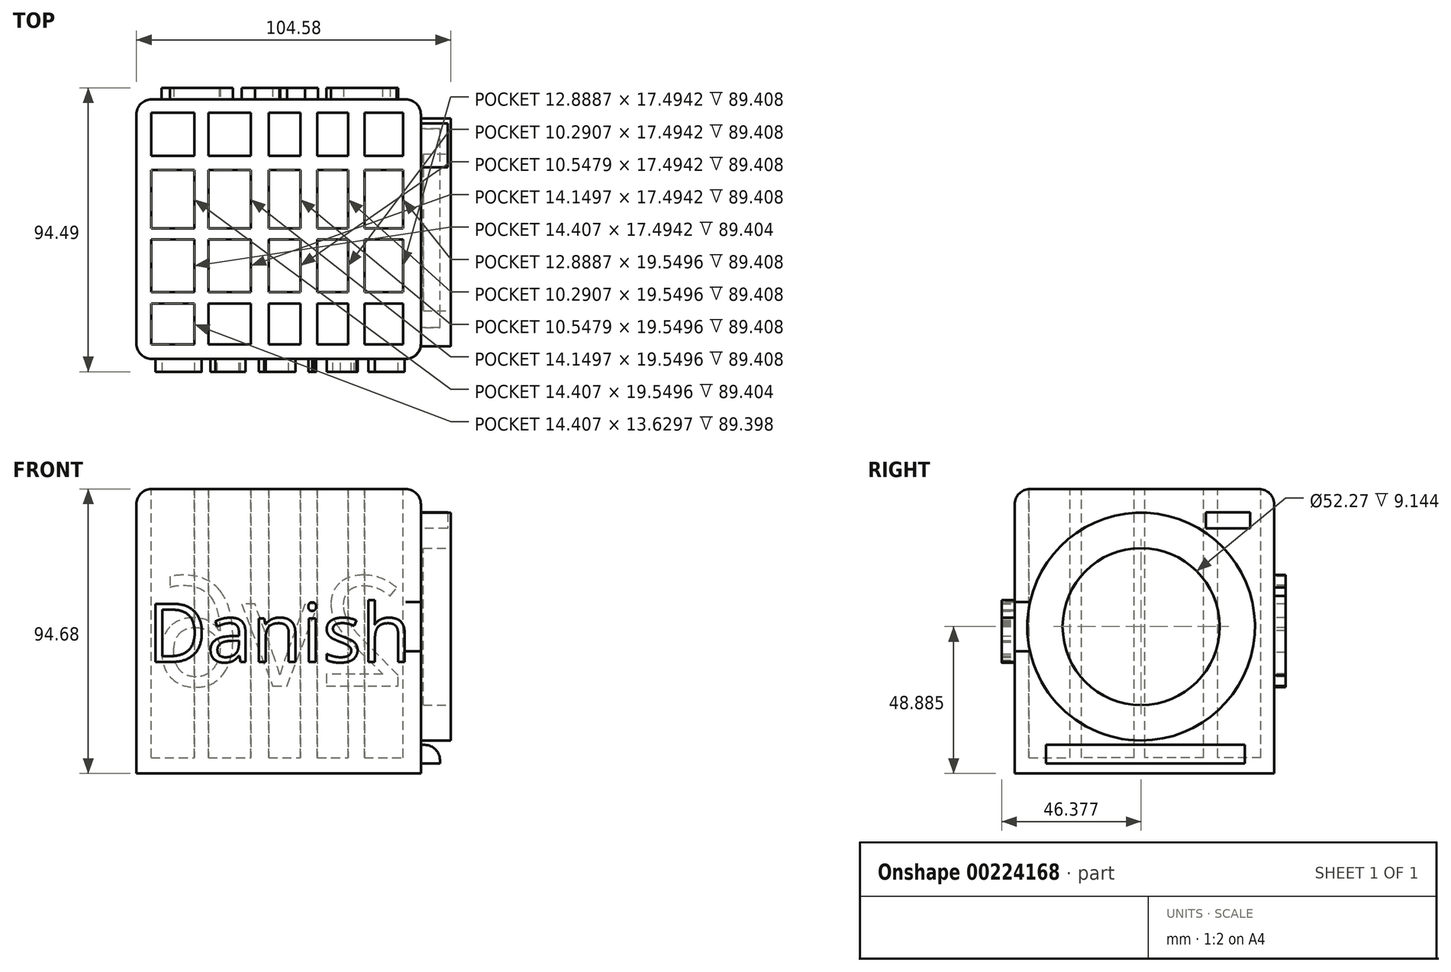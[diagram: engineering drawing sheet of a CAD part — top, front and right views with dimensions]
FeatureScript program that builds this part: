
annotation { "Feature Type Name" : "Feature", "Feature Type Description" : "" }
export const myFeature = defineFeature(function(context is Context, id is Id, definition is map)
    precondition{}
    {
        {
            var Q0;
            Q0=qCreatedBy(makeId("Front.planeOp"),FACE);
            var sketch = newSketch(context, id + "F0", { "sketchPlane" : qUnion([Q0])});
            skLineSegment(sketch, "E0.bottom", {"start": v(-44, 40.39) * mm, "end": v(50.68, 40.39) * mm});
            skLineSegment(sketch, "E0.top", {"start": v(-44, -54.29) * mm, "end": v(50.68, -54.29) * mm});
            skLineSegment(sketch, "E0.left", {"start": v(-44, 40.39) * mm, "end": v(-44, -54.29) * mm});
            skLineSegment(sketch, "E0.right", {"start": v(50.68, 40.39) * mm, "end": v(50.68, -54.29) * mm});
            skSolve(sketch);
        }
        {
            var Q0;
            Q0=makeQuery(id+"F0.imprint","IMPRINT",FACE,{"disambiguationData":[TD([[makeQuery(id+"F0.imprint","IMPRINT",EDGE,{"derivedFrom":sQuery(id+"F0.wireOp",EDGE,"E0.bottom")}),-1.0]])]});
            extrude(context, id + "F1", {"entities" : qUnion([Q0]), "depth" : 50.3 * mm});
        }
        {
            var Q0;
            Q0=makeQuery(id+"F1.opExtrude","CAP_FACE",FACE,{"disambiguationData":[OSD([sQuery(id+"F0.wireOp",EDGE,"E0.bottom"),sQuery(id+"F0.wireOp",EDGE,"E0.top"),sQuery(id+"F0.wireOp",EDGE,"E0.left"),sQuery(id+"F0.wireOp",EDGE,"E0.right")])],"isStart":true});
            extrude(context, id + "F2", {"entities" : qUnion([Q0]), "operationType" : NewBodyOperationType.ADD, "depth" : 36.07 * mm});
        }
        {
            var Q0;
            {var subQ0=sQuery(id+"F0.wireOp",EDGE,"E0.bottom");Q0=makeQuery(id+"F2.boolean.opBoolean","MERGE",FACE,{"derivedFrom":[makeQuery(id+"F1.opExtrude","SWEPT_FACE",FACE,{"disambiguationData":[OSD([subQ0])]}),makeQuery(id+"F2.opExtrude","SWEPT_FACE",FACE,{"disambiguationData":[OSD([subQ0])]})]});}
            var sketch = newSketch(context, id + "F3", { "sketchPlane" : qUnion([Q0])});
            skLineSegment(sketch, "E1.bottom", {"start": v(-39.1, 31.64) * mm, "end": v(44.79, 31.64) * mm});
            skLineSegment(sketch, "E1.top", {"start": v(-39.1, -45.53) * mm, "end": v(44.79, -45.53) * mm});
            skLineSegment(sketch, "E1.left", {"start": v(-39.1, 31.64) * mm, "end": v(-39.1, -45.53) * mm});
            skLineSegment(sketch, "E1.right", {"start": v(44.79, 31.64) * mm, "end": v(44.79, -45.53) * mm});
            skSolve(sketch);
        }
        {
            var Q0;
            Q0=makeQuery(id+"F3.imprint","IMPRINT",FACE,{"disambiguationData":[TD([[makeQuery(id+"F3.imprint","IMPRINT",EDGE,{"derivedFrom":sQuery(id+"F3.wireOp",EDGE,"E1.bottom")}),-1.0]])]});
            extrude(context, id + "F4", {"entities" : qUnion([Q0]), "operationType" : NewBodyOperationType.REMOVE, "oppositeDirection" : true, "depth" : 89.4 * mm});
        }
        {
            var Q0;
            Q0=makeQuery(id+"F4.boolean.opBoolean","COPY",FACE,{"derivedFrom":makeQuery(id+"F4.opExtrude","CAP_FACE",FACE,{"disambiguationData":[OSD([sQuery(id+"F3.wireOp",EDGE,"E1.bottom"),sQuery(id+"F3.wireOp",EDGE,"E1.top"),sQuery(id+"F3.wireOp",EDGE,"E1.left"),sQuery(id+"F3.wireOp",EDGE,"E1.right")])],"isStart":false})});
            var sketch = newSketch(context, id + "F5", { "sketchPlane" : qUnion([Q0])});
            skLineSegment(sketch, "E2.bottom", {"start": v(-24.7, -45.53) * mm, "end": v(-20.07, -45.53) * mm});
            skLineSegment(sketch, "E2.top", {"start": v(-24.7, 31.64) * mm, "end": v(-20.07, 31.64) * mm});
            skLineSegment(sketch, "E2.left", {"start": v(-24.7, -45.53) * mm, "end": v(-24.7, 31.64) * mm});
            skLineSegment(sketch, "E2.right", {"start": v(-20.07, -45.53) * mm, "end": v(-20.07, 31.64) * mm});
            skLineSegment(sketch, "E3.bottom", {"start": v(0, -45.53) * mm, "end": v(-5.92, -45.53) * mm});
            skLineSegment(sketch, "E3.top", {"start": v(0, 31.64) * mm, "end": v(-5.92, 31.64) * mm});
            skLineSegment(sketch, "E3.left", {"start": v(0, -45.53) * mm, "end": v(0, 31.64) * mm});
            skLineSegment(sketch, "E3.right", {"start": v(-5.92, -45.53) * mm, "end": v(-5.92, 31.64) * mm});
            skLineSegment(sketch, "E4.bottom", {"start": v(16.2, -45.53) * mm, "end": v(10.55, -45.53) * mm});
            skLineSegment(sketch, "E4.top", {"start": v(16.2, 31.64) * mm, "end": v(10.55, 31.64) * mm});
            skLineSegment(sketch, "E4.left", {"start": v(16.2, -45.53) * mm, "end": v(16.2, 31.64) * mm});
            skLineSegment(sketch, "E4.right", {"start": v(10.55, -45.53) * mm, "end": v(10.55, 31.64) * mm});
            skLineSegment(sketch, "E5.bottom", {"start": v(31.9, -45.53) * mm, "end": v(26.5, -45.53) * mm});
            skLineSegment(sketch, "E5.top", {"start": v(31.9, 31.64) * mm, "end": v(26.5, 31.64) * mm});
            skLineSegment(sketch, "E5.left", {"start": v(31.9, -45.53) * mm, "end": v(31.9, 31.64) * mm});
            skLineSegment(sketch, "E5.right", {"start": v(26.5, -45.53) * mm, "end": v(26.5, 31.64) * mm});
            skSolve(sketch);
        }
        {
            var Q0;
            Q0=makeQuery(id+"F5.imprint","IMPRINT",FACE,{"disambiguationData":[TD([[makeQuery(id+"F5.imprint","IMPRINT",EDGE,{"derivedFrom":sQuery(id+"F5.wireOp",EDGE,"E2.bottom")}),1.0]])]});
            var Q1;
            Q1=makeQuery(id+"F5.imprint","IMPRINT",FACE,{"disambiguationData":[TD([[makeQuery(id+"F5.imprint","IMPRINT",EDGE,{"derivedFrom":sQuery(id+"F5.wireOp",EDGE,"E3.bottom")}),1.0]])]});
            var Q2;
            Q2=makeQuery(id+"F5.imprint","IMPRINT",FACE,{"disambiguationData":[TD([[makeQuery(id+"F5.imprint","IMPRINT",EDGE,{"derivedFrom":sQuery(id+"F5.wireOp",EDGE,"E4.bottom")}),1.0]])]});
            var Q3;
            Q3=makeQuery(id+"F5.imprint","IMPRINT",FACE,{"disambiguationData":[TD([[makeQuery(id+"F5.imprint","IMPRINT",EDGE,{"derivedFrom":sQuery(id+"F5.wireOp",EDGE,"E5.bottom")}),1.0]])]});
            extrude(context, id + "F6", {"entities" : qUnion([Q0, Q1, Q2, Q3]), "operationType" : NewBodyOperationType.ADD, "depth" : 89.4 * mm});
        }
        {
            var Q0;
            {var subQ0=sQuery(id+"F0.wireOp",EDGE,"E0.bottom");Q0=makeQuery(id+"F6.boolean.opBoolean","MERGE",FACE,{"derivedFrom":[makeQuery(id+"F2.boolean.opBoolean","MERGE",FACE,{"derivedFrom":[makeQuery(id+"F1.opExtrude","SWEPT_FACE",FACE,{"disambiguationData":[OSD([subQ0])]}),makeQuery(id+"F2.opExtrude","SWEPT_FACE",FACE,{"disambiguationData":[OSD([subQ0])]})]}),makeQuery(id+"F6.opExtrude","CAP_FACE",FACE,{"disambiguationData":[OSD([sQuery(id+"F5.wireOp",EDGE,"E2.bottom"),sQuery(id+"F5.wireOp",EDGE,"E2.top"),sQuery(id+"F5.wireOp",EDGE,"E2.left"),sQuery(id+"F5.wireOp",EDGE,"E2.right")])],"isStart":false}),makeQuery(id+"F6.opExtrude","CAP_FACE",FACE,{"disambiguationData":[OSD([sQuery(id+"F5.wireOp",EDGE,"E3.bottom"),sQuery(id+"F5.wireOp",EDGE,"E3.top"),sQuery(id+"F5.wireOp",EDGE,"E3.left"),sQuery(id+"F5.wireOp",EDGE,"E3.right")])],"isStart":false}),makeQuery(id+"F6.opExtrude","CAP_FACE",FACE,{"disambiguationData":[OSD([sQuery(id+"F5.wireOp",EDGE,"E4.bottom"),sQuery(id+"F5.wireOp",EDGE,"E4.top"),sQuery(id+"F5.wireOp",EDGE,"E4.left"),sQuery(id+"F5.wireOp",EDGE,"E4.right")])],"isStart":false}),makeQuery(id+"F6.opExtrude","CAP_FACE",FACE,{"disambiguationData":[OSD([sQuery(id+"F5.wireOp",EDGE,"E5.bottom"),sQuery(id+"F5.wireOp",EDGE,"E5.top"),sQuery(id+"F5.wireOp",EDGE,"E5.left"),sQuery(id+"F5.wireOp",EDGE,"E5.right")])],"isStart":false})]});}
            var sketch = newSketch(context, id + "F7", { "sketchPlane" : qUnion([Q0])});
            skLineSegment(sketch, "E6.bottom", {"start": v(-39.1, 17.23) * mm, "end": v(44.79, 17.23) * mm});
            skLineSegment(sketch, "E6.top", {"start": v(-39.1, 12.6) * mm, "end": v(44.79, 12.6) * mm});
            skLineSegment(sketch, "E6.left", {"start": v(-39.1, 17.23) * mm, "end": v(-39.1, 12.6) * mm});
            skLineSegment(sketch, "E6.right", {"start": v(44.79, 17.23) * mm, "end": v(44.79, 12.6) * mm});
            skLineSegment(sketch, "E7.bottom", {"start": v(-39.1, -6.95) * mm, "end": v(47.08, -6.95) * mm});
            skLineSegment(sketch, "E7.top", {"start": v(-39.1, -10.55) * mm, "end": v(47.08, -10.55) * mm});
            skLineSegment(sketch, "E7.left", {"start": v(-39.1, -6.95) * mm, "end": v(-39.1, -10.55) * mm});
            skLineSegment(sketch, "E7.right", {"start": v(47.08, -6.95) * mm, "end": v(47.08, -10.55) * mm});
            skLineSegment(sketch, "E8.bottom", {"start": v(-39.1, -28.04) * mm, "end": v(44.79, -28.04) * mm});
            skLineSegment(sketch, "E8.top", {"start": v(-39.1, -31.9) * mm, "end": v(44.79, -31.9) * mm});
            skLineSegment(sketch, "E8.left", {"start": v(-39.1, -28.04) * mm, "end": v(-39.1, -31.9) * mm});
            skLineSegment(sketch, "E8.right", {"start": v(44.79, -28.04) * mm, "end": v(44.79, -31.9) * mm});
            skSolve(sketch);
        }
        {
            var Q0;
            {var subQ0=sQuery(id+"F7.wireOp",EDGE,"E6.left");Q0=makeQuery(id+"F7.imprint","IMPRINT",FACE,{"disambiguationData":[TD([[makeQuery(id+"F7.imprint","IMPRINT",EDGE,{"derivedFrom":subQ0}),1.0]])]});}
            var Q1;
            {var subQ0=sQuery(id+"F7.wireOp",EDGE,"E6.bottom");var subQ1=makeQuery(id+"F6.opExtrude","CAP_EDGE",EDGE,{"disambiguationData":[OSD([sQuery(id+"F5.wireOp",EDGE,"E2.right")])],"isStart":false});var subQ2=makeQuery(id+"F7.imprint","INTERSECT",VERTEX,{"derivedFrom":[subQ1,subQ0]});Q1=makeQuery(id+"F7.imprint","IMPRINT",FACE,{"disambiguationData":[TD([[makeQuery(id+"F7.imprint","IMPRINT",EDGE,{"disambiguationData":[TD([[subQ2,-1.0]])],"derivedFrom":subQ0}),-1.0]])]});}
            var Q2;
            {var subQ0=sQuery(id+"F7.wireOp",EDGE,"E6.bottom");var subQ1=makeQuery(id+"F6.opExtrude","CAP_EDGE",EDGE,{"disambiguationData":[OSD([sQuery(id+"F5.wireOp",EDGE,"E3.left")])],"isStart":false});var subQ2=makeQuery(id+"F7.imprint","INTERSECT",VERTEX,{"derivedFrom":[subQ1,subQ0]});Q2=makeQuery(id+"F7.imprint","IMPRINT",FACE,{"disambiguationData":[TD([[makeQuery(id+"F7.imprint","IMPRINT",EDGE,{"disambiguationData":[TD([[subQ2,-1.0]])],"derivedFrom":subQ0}),-1.0]])]});}
            var Q3;
            {var subQ0=sQuery(id+"F7.wireOp",EDGE,"E6.bottom");var subQ1=makeQuery(id+"F6.opExtrude","CAP_EDGE",EDGE,{"disambiguationData":[OSD([sQuery(id+"F5.wireOp",EDGE,"E4.left")])],"isStart":false});var subQ2=makeQuery(id+"F7.imprint","INTERSECT",VERTEX,{"derivedFrom":[subQ1,subQ0]});Q3=makeQuery(id+"F7.imprint","IMPRINT",FACE,{"disambiguationData":[TD([[makeQuery(id+"F7.imprint","IMPRINT",EDGE,{"disambiguationData":[TD([[subQ2,-1.0]])],"derivedFrom":subQ0}),-1.0]])]});}
            var Q4;
            {var subQ0=sQuery(id+"F7.wireOp",EDGE,"E6.right");Q4=makeQuery(id+"F7.imprint","IMPRINT",FACE,{"disambiguationData":[TD([[makeQuery(id+"F7.imprint","IMPRINT",EDGE,{"derivedFrom":subQ0}),-1.0]])]});}
            var Q5;
            {var subQ0=sQuery(id+"F7.wireOp",EDGE,"E7.bottom");var subQ1=makeQuery(id+"F6.opExtrude","CAP_EDGE",EDGE,{"disambiguationData":[OSD([sQuery(id+"F5.wireOp",EDGE,"E5.left")])],"isStart":false});var subQ2=makeQuery(id+"F7.imprint","INTERSECT",VERTEX,{"derivedFrom":[subQ1,subQ0]});Q5=makeQuery(id+"F7.imprint","IMPRINT",FACE,{"disambiguationData":[TD([[makeQuery(id+"F7.imprint","IMPRINT",EDGE,{"disambiguationData":[TD([[subQ2,-1.0]])],"derivedFrom":subQ0}),-1.0]])]});}
            var Q6;
            {var subQ0=sQuery(id+"F7.wireOp",EDGE,"E7.bottom");var subQ1=makeQuery(id+"F6.opExtrude","CAP_EDGE",EDGE,{"disambiguationData":[OSD([sQuery(id+"F5.wireOp",EDGE,"E4.left")])],"isStart":false});var subQ2=makeQuery(id+"F7.imprint","INTERSECT",VERTEX,{"derivedFrom":[subQ1,subQ0]});Q6=makeQuery(id+"F7.imprint","IMPRINT",FACE,{"disambiguationData":[TD([[makeQuery(id+"F7.imprint","IMPRINT",EDGE,{"disambiguationData":[TD([[subQ2,-1.0]])],"derivedFrom":subQ0}),-1.0]])]});}
            var Q7;
            {var subQ0=sQuery(id+"F7.wireOp",EDGE,"E7.bottom");var subQ1=makeQuery(id+"F6.opExtrude","CAP_EDGE",EDGE,{"disambiguationData":[OSD([sQuery(id+"F5.wireOp",EDGE,"E3.left")])],"isStart":false});var subQ2=makeQuery(id+"F7.imprint","INTERSECT",VERTEX,{"derivedFrom":[subQ1,subQ0]});Q7=makeQuery(id+"F7.imprint","IMPRINT",FACE,{"disambiguationData":[TD([[makeQuery(id+"F7.imprint","IMPRINT",EDGE,{"disambiguationData":[TD([[subQ2,-1.0]])],"derivedFrom":subQ0}),-1.0]])]});}
            var Q8;
            {var subQ0=sQuery(id+"F7.wireOp",EDGE,"E7.bottom");var subQ1=makeQuery(id+"F6.opExtrude","CAP_EDGE",EDGE,{"disambiguationData":[OSD([sQuery(id+"F5.wireOp",EDGE,"E2.right")])],"isStart":false});var subQ2=makeQuery(id+"F7.imprint","INTERSECT",VERTEX,{"derivedFrom":[subQ1,subQ0]});Q8=makeQuery(id+"F7.imprint","IMPRINT",FACE,{"disambiguationData":[TD([[makeQuery(id+"F7.imprint","IMPRINT",EDGE,{"disambiguationData":[TD([[subQ2,-1.0]])],"derivedFrom":subQ0}),-1.0]])]});}
            var Q9;
            {var subQ0=sQuery(id+"F7.wireOp",EDGE,"E7.left");Q9=makeQuery(id+"F7.imprint","IMPRINT",FACE,{"disambiguationData":[TD([[makeQuery(id+"F7.imprint","IMPRINT",EDGE,{"derivedFrom":subQ0}),1.0]])]});}
            var Q10;
            {var subQ0=sQuery(id+"F7.wireOp",EDGE,"E8.left");Q10=makeQuery(id+"F7.imprint","IMPRINT",FACE,{"disambiguationData":[TD([[makeQuery(id+"F7.imprint","IMPRINT",EDGE,{"derivedFrom":subQ0}),1.0]])]});}
            var Q11;
            {var subQ0=sQuery(id+"F7.wireOp",EDGE,"E8.bottom");var subQ1=makeQuery(id+"F6.opExtrude","CAP_EDGE",EDGE,{"disambiguationData":[OSD([sQuery(id+"F5.wireOp",EDGE,"E2.right")])],"isStart":false});var subQ2=makeQuery(id+"F7.imprint","INTERSECT",VERTEX,{"derivedFrom":[subQ1,subQ0]});Q11=makeQuery(id+"F7.imprint","IMPRINT",FACE,{"disambiguationData":[TD([[makeQuery(id+"F7.imprint","IMPRINT",EDGE,{"disambiguationData":[TD([[subQ2,-1.0]])],"derivedFrom":subQ0}),-1.0]])]});}
            var Q12;
            {var subQ0=sQuery(id+"F7.wireOp",EDGE,"E8.bottom");var subQ1=makeQuery(id+"F6.opExtrude","CAP_EDGE",EDGE,{"disambiguationData":[OSD([sQuery(id+"F5.wireOp",EDGE,"E3.left")])],"isStart":false});var subQ2=makeQuery(id+"F7.imprint","INTERSECT",VERTEX,{"derivedFrom":[subQ1,subQ0]});Q12=makeQuery(id+"F7.imprint","IMPRINT",FACE,{"disambiguationData":[TD([[makeQuery(id+"F7.imprint","IMPRINT",EDGE,{"disambiguationData":[TD([[subQ2,-1.0]])],"derivedFrom":subQ0}),-1.0]])]});}
            var Q13;
            {var subQ0=sQuery(id+"F7.wireOp",EDGE,"E8.bottom");var subQ1=makeQuery(id+"F6.opExtrude","CAP_EDGE",EDGE,{"disambiguationData":[OSD([sQuery(id+"F5.wireOp",EDGE,"E4.left")])],"isStart":false});var subQ2=makeQuery(id+"F7.imprint","INTERSECT",VERTEX,{"derivedFrom":[subQ1,subQ0]});Q13=makeQuery(id+"F7.imprint","IMPRINT",FACE,{"disambiguationData":[TD([[makeQuery(id+"F7.imprint","IMPRINT",EDGE,{"disambiguationData":[TD([[subQ2,-1.0]])],"derivedFrom":subQ0}),-1.0]])]});}
            var Q14;
            {var subQ0=sQuery(id+"F7.wireOp",EDGE,"E8.right");Q14=makeQuery(id+"F7.imprint","IMPRINT",FACE,{"disambiguationData":[TD([[makeQuery(id+"F7.imprint","IMPRINT",EDGE,{"derivedFrom":subQ0}),-1.0]])]});}
            extrude(context, id + "F8", {"entities" : qUnion([Q0, Q1, Q2, Q3, Q4, Q5, Q6, Q7, Q8, Q9, Q10, Q11, Q12, Q13, Q14]), "operationType" : NewBodyOperationType.ADD, "oppositeDirection" : true, "depth" : 91.44 * mm});
        }
        {
            var Q0;
            {var subQ0=sQuery(id+"F0.wireOp",EDGE,"E0.right");Q0=makeQuery(id+"F2.boolean.opBoolean","MERGE",FACE,{"derivedFrom":[makeQuery(id+"F1.opExtrude","SWEPT_FACE",FACE,{"disambiguationData":[OSD([subQ0])]}),makeQuery(id+"F2.opExtrude","SWEPT_FACE",FACE,{"disambiguationData":[OSD([subQ0])]})]});}
            var sketch = newSketch(context, id + "F9", { "sketchPlane" : qUnion([Q0])});
            skCircle(sketch, "E9", {"center": v(-8.23, -5.4) * mm, "radius": 37.89 * mm});
            skSolve(sketch);
        }
        {
            var Q0;
            Q0=makeQuery(id+"F9.imprint","IMPRINT",FACE,{"disambiguationData":[TD([[makeQuery(id+"F9.imprint","IMPRINT",EDGE,{"derivedFrom":sQuery(id+"F9.wireOp",EDGE,"E9")}),1.0]])]});
            extrude(context, id + "F10", {"entities" : qUnion([Q0]), "operationType" : NewBodyOperationType.ADD, "depth" : 9.9 * mm});
        }
        {
            var Q0;
            Q0=makeQuery(id+"F2.opExtrude","CAP_EDGE",EDGE,{"disambiguationData":[OSD([sQuery(id+"F0.wireOp",EDGE,"E0.bottom")])],"isStart":false});
            fillet(context, id + "F11", {"entities" : qUnion([Q0]), "radius" : 5.08 * mm, "tangentPropagation" : true, "allowEdgeOverflow" : false});
        }
        {
            var Q0;
            {var subQ0=sQuery(id+"F0.wireOp",EDGE,"E0.right");var subQ1=sQuery(id+"F0.wireOp",EDGE,"E0.bottom");Q0=makeQuery(id+"F2.boolean.opBoolean","MERGE",EDGE,{"derivedFrom":[makeQuery(id+"F1.opExtrude","SWEPT_EDGE",EDGE,{"disambiguationData":[OSD([subQ1,subQ0])]}),makeQuery(id+"F2.opExtrude","SWEPT_EDGE",EDGE,{"disambiguationData":[OSD([subQ1,subQ0])]})]});}
            fillet(context, id + "F12", {"entities" : qUnion([Q0]), "radius" : 5.08 * mm, "tangentPropagation" : true, "allowEdgeOverflow" : false});
        }
        {
            var Q0;
            Q0=makeQuery(id+"F1.opExtrude","CAP_EDGE",EDGE,{"disambiguationData":[OSD([sQuery(id+"F0.wireOp",EDGE,"E0.bottom")])],"isStart":false});
            fillet(context, id + "F13", {"entities" : qUnion([Q0]), "radius" : 5.08 * mm, "tangentPropagation" : true, "allowEdgeOverflow" : false});
        }
        {
            var Q0;
            {var subQ0=sQuery(id+"F0.wireOp",EDGE,"E0.left");var subQ1=sQuery(id+"F0.wireOp",EDGE,"E0.bottom");Q0=makeQuery(id+"F2.boolean.opBoolean","MERGE",EDGE,{"derivedFrom":[makeQuery(id+"F1.opExtrude","SWEPT_EDGE",EDGE,{"disambiguationData":[OSD([subQ1,subQ0])]}),makeQuery(id+"F2.opExtrude","SWEPT_EDGE",EDGE,{"disambiguationData":[OSD([subQ1,subQ0])]})]});}
            fillet(context, id + "F14", {"entities" : qUnion([Q0]), "radius" : 5.08 * mm, "tangentPropagation" : true, "allowEdgeOverflow" : false});
        }
        {
            var Q0;
            Q0=makeQuery(id+"F10.opExtrude","CAP_FACE",FACE,{"disambiguationData":[OSD([sQuery(id+"F9.wireOp",EDGE,"E9")])],"isStart":false});
            var sketch = newSketch(context, id + "F15", { "sketchPlane" : qUnion([Q0])});
            skCircle(sketch, "E10", {"center": v(-8.23, -5.4) * mm, "radius": 26.14 * mm});
            skSolve(sketch);
        }
        {
            var Q0;
            Q0=makeQuery(id+"F15.imprint","IMPRINT",FACE,{"disambiguationData":[TD([[makeQuery(id+"F15.imprint","IMPRINT",EDGE,{"derivedFrom":sQuery(id+"F15.wireOp",EDGE,"E10")}),1.0]])]});
            extrude(context, id + "F16", {"entities" : qUnion([Q0]), "operationType" : NewBodyOperationType.REMOVE, "oppositeDirection" : true, "depth" : 9.14 * mm});
        }
        {
            var Q0;
            {var subQ0=sQuery(id+"F0.wireOp",EDGE,"E0.right");Q0=makeQuery(id+"F2.boolean.opBoolean","MERGE",FACE,{"derivedFrom":[makeQuery(id+"F1.opExtrude","SWEPT_FACE",FACE,{"disambiguationData":[OSD([subQ0])]}),makeQuery(id+"F2.opExtrude","SWEPT_FACE",FACE,{"disambiguationData":[OSD([subQ0])]})]});}
            var sketch = newSketch(context, id + "F17", { "sketchPlane" : qUnion([Q0])});
            skLineSegment(sketch, "E11.bottom", {"start": v(13.38, 32.67) * mm, "end": v(28.04, 32.67) * mm});
            skLineSegment(sketch, "E11.top", {"start": v(13.38, 27.27) * mm, "end": v(28.04, 27.27) * mm});
            skLineSegment(sketch, "E11.left", {"start": v(13.38, 32.67) * mm, "end": v(13.38, 27.27) * mm});
            skLineSegment(sketch, "E11.right", {"start": v(28.04, 32.67) * mm, "end": v(28.04, 27.27) * mm});
            skSolve(sketch);
        }
        {
            var Q0;
            Q0=makeQuery(id+"F17.imprint","IMPRINT",FACE,{"disambiguationData":[TD([[makeQuery(id+"F17.imprint","IMPRINT",EDGE,{"derivedFrom":sQuery(id+"F17.wireOp",EDGE,"E11.bottom")}),-1.0]])]});
            extrude(context, id + "F18", {"entities" : qUnion([Q0]), "operationType" : NewBodyOperationType.ADD, "depth" : 8.9 * mm});
        }
        {
            var Q0;
            Q0=makeQuery(id+"F1.opExtrude","CAP_FACE",FACE,{"disambiguationData":[OSD([sQuery(id+"F0.wireOp",EDGE,"E0.bottom"),sQuery(id+"F0.wireOp",EDGE,"E0.top"),sQuery(id+"F0.wireOp",EDGE,"E0.left"),sQuery(id+"F0.wireOp",EDGE,"E0.right")])],"isStart":false});
            var sketch = newSketch(context, id + "F19", { "sketchPlane" : qUnion([Q0])});
            skText(sketch, "E12", { "text": "Danish", "fontName": "OpenSans-Regular.ttf"});
            const initialGuessF19  = {"E12": [-0.04031, -0.01715, 1, 0, 0.01949]};
            skSetInitialGuess(sketch, initialGuessF19);
            skSolve(sketch);
        }
        {
            var Q0;
            Q0 = qSketchRegion(id + "F19", true);
            extrude(context, id + "F20", {"entities" : qUnion([Q0]), "operationType" : NewBodyOperationType.ADD, "depth" : 4.32 * mm});
        }
        {
            var Q0;
            Q0=makeQuery(id+"F2.opExtrude","CAP_FACE",FACE,{"disambiguationData":[OSD([sQuery(id+"F0.wireOp",EDGE,"E0.bottom"),sQuery(id+"F0.wireOp",EDGE,"E0.top"),sQuery(id+"F0.wireOp",EDGE,"E0.left"),sQuery(id+"F0.wireOp",EDGE,"E0.right")])],"isStart":false});
            var sketch = newSketch(context, id + "F21", { "sketchPlane" : qUnion([Q0])});
            skText(sketch, "E13", { "text": "2v6", "fontName": "OpenSans-Regular.ttf"});
            const initialGuessF21  = {"E13": [-0.0456, -0.0251, 1, 0, 0.03665]};
            skSetInitialGuess(sketch, initialGuessF21);
            skSolve(sketch);
        }
        {
            var Q0;
            Q0 = qSketchRegion(id + "F21", true);
            extrude(context, id + "F22", {"entities" : qUnion([Q0]), "operationType" : NewBodyOperationType.ADD, "depth" : 3.8 * mm});
        }
        {
            var Q0;
            {var subQ0=sQuery(id+"F0.wireOp",EDGE,"E0.right");Q0=makeQuery(id+"F2.boolean.opBoolean","MERGE",FACE,{"derivedFrom":[makeQuery(id+"F1.opExtrude","SWEPT_FACE",FACE,{"disambiguationData":[OSD([subQ0])]}),makeQuery(id+"F2.opExtrude","SWEPT_FACE",FACE,{"disambiguationData":[OSD([subQ0])]})]});}
            var sketch = newSketch(context, id + "F23", { "sketchPlane" : qUnion([Q0])});
            skLineSegment(sketch, "E14.bottom", {"start": v(-39.88, -44.77) * mm, "end": v(26.24, -44.77) * mm});
            skLineSegment(sketch, "E14.top", {"start": v(-39.88, -50.94) * mm, "end": v(26.24, -50.94) * mm});
            skLineSegment(sketch, "E14.left", {"start": v(-39.88, -44.77) * mm, "end": v(-39.88, -50.94) * mm});
            skLineSegment(sketch, "E14.right", {"start": v(26.24, -44.77) * mm, "end": v(26.24, -50.94) * mm});
            skSolve(sketch);
        }
        {
            var Q0;
            Q0=makeQuery(id+"F23.imprint","IMPRINT",FACE,{"disambiguationData":[TD([[makeQuery(id+"F23.imprint","IMPRINT",EDGE,{"derivedFrom":sQuery(id+"F23.wireOp",EDGE,"E14.bottom")}),-1.0]])]});
            extrude(context, id + "F24", {"entities" : qUnion([Q0]), "operationType" : NewBodyOperationType.ADD, "depth" : 6.35 * mm});
        }
        {
            var Q0;
            Q0=makeQuery(id+"F24.opExtrude","CAP_EDGE",EDGE,{"disambiguationData":[OSD([sQuery(id+"F23.wireOp",EDGE,"E14.bottom")])],"isStart":false});
            fillet(context, id + "F25", {"entities" : qUnion([Q0]), "radius" : 5.08 * mm, "tangentPropagation" : true, "allowEdgeOverflow" : false});
        }
    });
